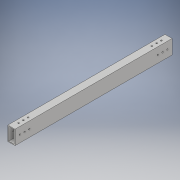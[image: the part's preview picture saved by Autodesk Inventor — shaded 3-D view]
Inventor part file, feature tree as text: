
AUTODESK INVENTOR PART (.ipt)
format: ipt  version: 2019 (Build 230136000, 136)  size: 168,960 bytes
history: native  units: mm
features: sketch x4, extrude x2, hole x2, other x1
ambient origin geometry x8: Origin, YZ Plane, XZ Plane, XY Plane, X Axis, Y Axis, Z Axis, Center Point
bodies: Body1 (feature_tree)
feature tree (9):
  other  "ソリッド1"
  extrude  "押し出し1"  Depth=15.0mm
  hole  "穴1"  [1 undecoded]
  hole  "穴2"  [1 undecoded]
  extrude  "押し出し2"  Depth=3.0mm
  sketch  "スケッチ1"
  sketch  "スケッチ2"
  sketch  "スケッチ3"
  sketch  "スケッチ4"
note: 2 required parameter values undecoded (feature->parameter linkage not recoverable at this tier; creation-order binding heuristic only, values carry confidence <= 0.55)
